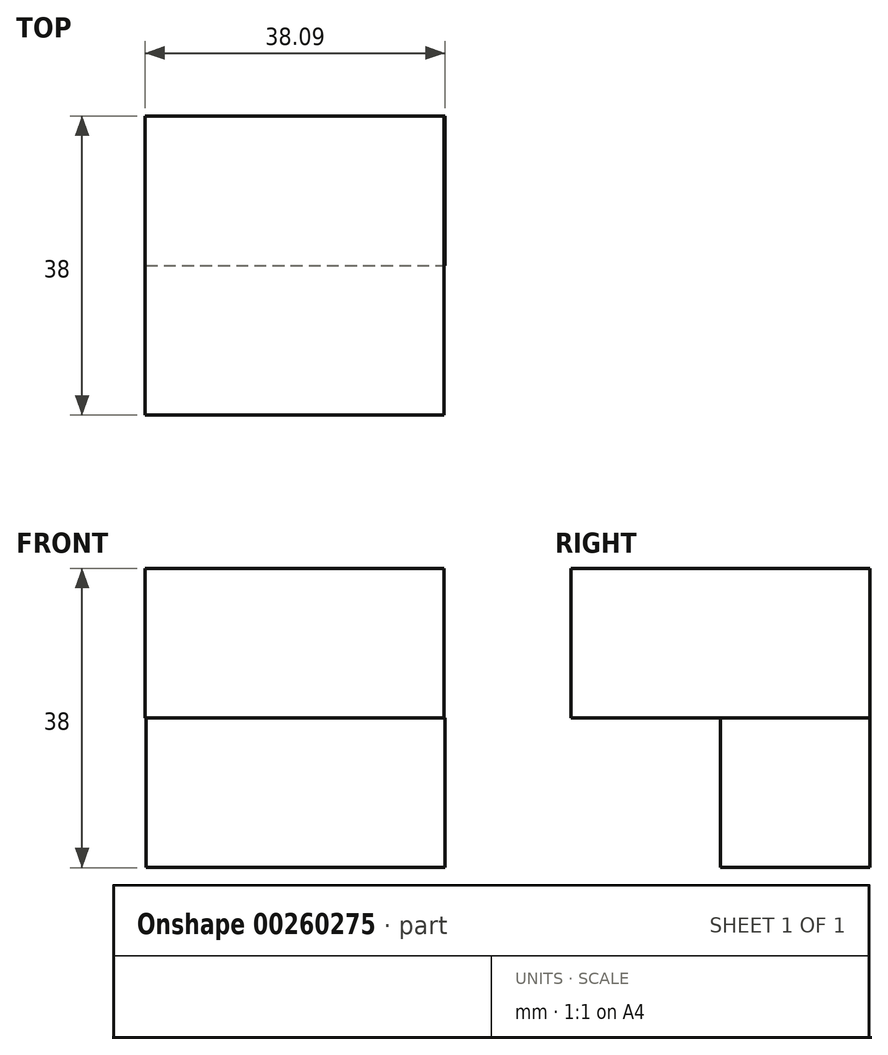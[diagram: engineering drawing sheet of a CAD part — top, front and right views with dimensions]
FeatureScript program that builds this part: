
annotation { "Feature Type Name" : "Feature", "Feature Type Description" : "" }
export const myFeature = defineFeature(function(context is Context, id is Id, definition is map)
    precondition{}
    {
        {
            var Q0;
            Q0=qCreatedBy(makeId("Top.planeOp"),FACE);
            var sketch = newSketch(context, id + "F0", { "sketchPlane" : qUnion([Q0])});
            skLineSegment(sketch, "E0.bottom", {"start": v(-19, 19) * mm, "end": v(19, 19) * mm});
            skLineSegment(sketch, "E0.top", {"start": v(-19, -19) * mm, "end": v(19, -19) * mm});
            skLineSegment(sketch, "E0.left", {"start": v(-19, 19) * mm, "end": v(-19, -19) * mm});
            skLineSegment(sketch, "E0.right", {"start": v(19, 19) * mm, "end": v(19, -19) * mm});
            skPoint(sketch, "E0.middle", {"position": v(0, 0) * mm});
            skSolve(sketch);
        }
        {
            var Q0;
            Q0 = qSketchRegion(id + "F0", true);
            extrude(context, id + "F1", {"entities" : qUnion([Q0]), "depth" : 19 * mm});
        }
        {
            var Q0;
            Q0=qCreatedBy(makeId("Top.planeOp"),FACE);
            var sketch = newSketch(context, id + "F2", { "sketchPlane" : qUnion([Q0])});
            skLineSegment(sketch, "E1.bottom", {"start": v(-18.9, 0) * mm, "end": v(19.1, 0) * mm});
            skLineSegment(sketch, "E1.top", {"start": v(-18.9, 19) * mm, "end": v(19.1, 19) * mm});
            skLineSegment(sketch, "E1.left", {"start": v(-18.9, 0) * mm, "end": v(-18.9, 19) * mm});
            skLineSegment(sketch, "E1.right", {"start": v(19.1, 0) * mm, "end": v(19.1, 19) * mm});
            skSolve(sketch);
        }
        {
            var Q0;
            Q0 = qSketchRegion(id + "F2", true);
            extrude(context, id + "F3", {"entities" : qUnion([Q0]), "operationType" : NewBodyOperationType.ADD, "oppositeDirection" : true, "depth" : 19 * mm});
        }
    });
